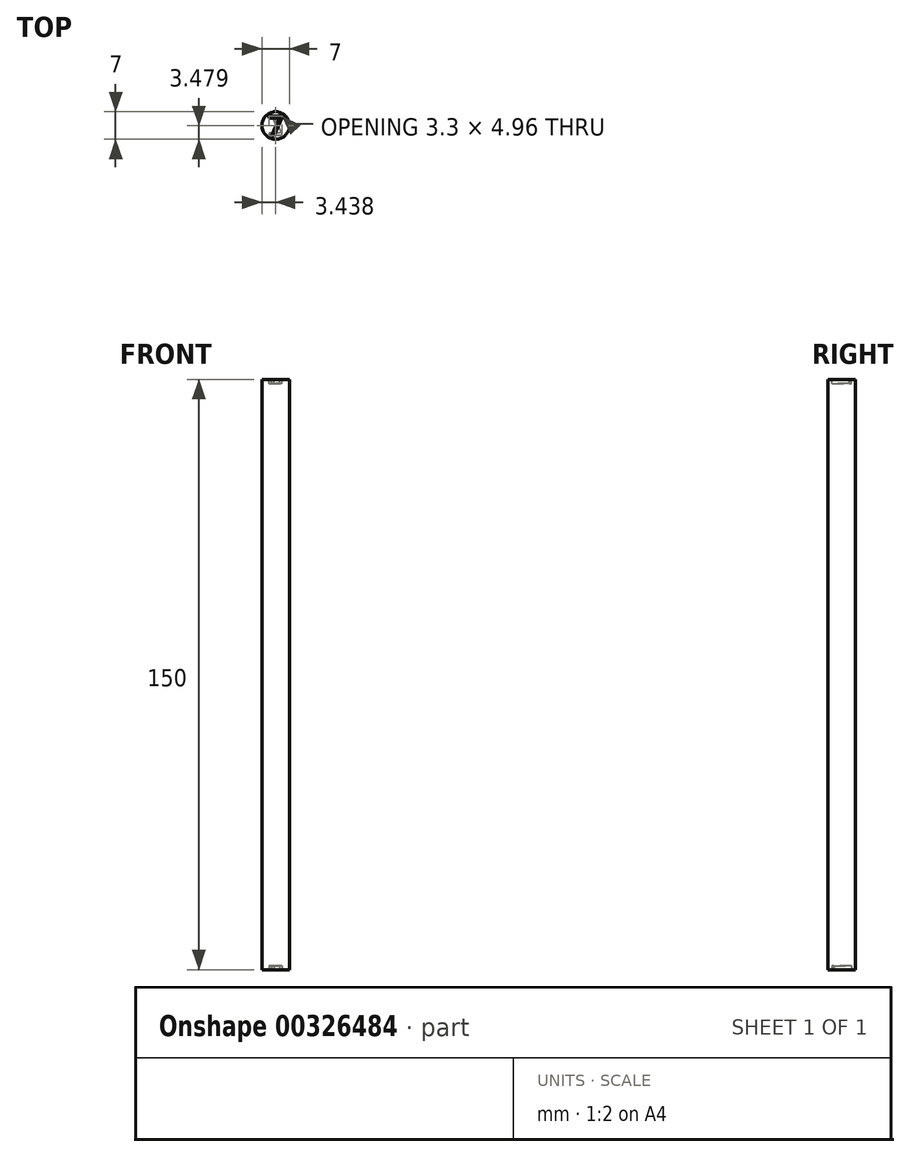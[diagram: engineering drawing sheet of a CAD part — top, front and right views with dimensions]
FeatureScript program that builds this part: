
annotation { "Feature Type Name" : "Feature", "Feature Type Description" : "" }
export const myFeature = defineFeature(function(context is Context, id is Id, definition is map)
    precondition{}
    {
        {
            var Q0;
            Q0=qCreatedBy(makeId("Top.planeOp"),FACE);
            var sketch = newSketch(context, id + "F0", { "sketchPlane" : qUnion([Q0])});
            skCircle(sketch, "E0", {"center": v(0, 0) * mm, "radius": 3.5 * mm});
            skSolve(sketch);
        }
        {
            var Q0;
            Q0=makeQuery(id+"F0.imprint","IMPRINT",FACE,{"disambiguationData":[TD([[makeQuery(id+"F0.imprint","IMPRINT",EDGE,{"derivedFrom":sQuery(id+"F0.wireOp",EDGE,"E0")}),1.0]])]});
            extrude(context, id + "F1", {"entities" : qUnion([Q0]), "depth" : 150 * mm});
        }
        {
            var Q0;
            Q0=makeQuery(id+"F1.opExtrude","CAP_FACE",FACE,{"disambiguationData":[OSD([sQuery(id+"F0.wireOp",EDGE,"E0")])],"isStart":true});
            var sketch = newSketch(context, id + "F2", { "sketchPlane" : qUnion([Q0])});
            skText(sketch, "E1", { "text": "7", "fontName": "OpenSans-Regular.ttf"});
            const initialGuessF2  = {"E1": [-0.00203, -0.0025, 1, 0, 0.005]};
            skSetInitialGuess(sketch, initialGuessF2);
            skSolve(sketch);
        }
        {
            var Q0;
            Q0=makeQuery(id+"F2.imprint","IMPRINT",FACE,{"disambiguationData":[TD([[makeQuery(id+"F2.imprint","IMPRINT",EDGE,{"derivedFrom":sQuery(id+"F2.wireOp",EDGE,"E1.sketch_text.stroke-0")}),-1.0]])]});
            extrude(context, id + "F3", {"entities" : qUnion([Q0]), "operationType" : NewBodyOperationType.REMOVE, "oppositeDirection" : true, "depth" : 1 * mm});
        }
        {
            var Q0;
            Q0=makeQuery(id+"F1.opExtrude","CAP_FACE",FACE,{"disambiguationData":[OSD([sQuery(id+"F0.wireOp",EDGE,"E0")])],"isStart":false});
            var sketch = newSketch(context, id + "F4", { "sketchPlane" : qUnion([Q0])});
            skText(sketch, "E2", { "text": "7", "fontName": "OpenSans-Regular.ttf"});
            const initialGuessF4  = {"E2": [-0.00203, -0.0025, 1, 0, 0.005]};
            skSetInitialGuess(sketch, initialGuessF4);
            skSolve(sketch);
        }
        {
            var Q0;
            Q0 = qSketchRegion(id + "F4", true);
            extrude(context, id + "F5", {"entities" : qUnion([Q0]), "operationType" : NewBodyOperationType.REMOVE, "oppositeDirection" : true, "depth" : 1 * mm});
        }
    });
